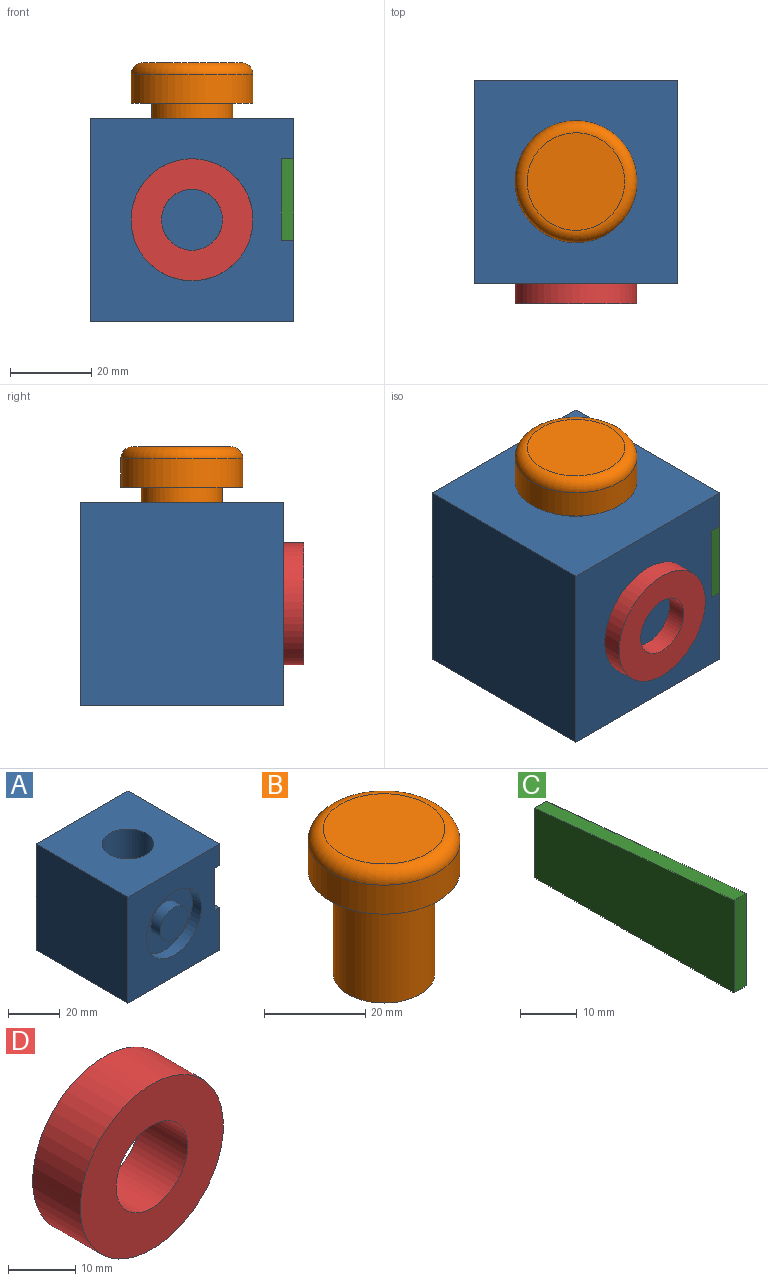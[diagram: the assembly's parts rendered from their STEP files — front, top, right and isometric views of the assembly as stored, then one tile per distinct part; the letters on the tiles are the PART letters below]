
ASSEMBLY  parts=4 mates=3
PART A: 16 faces, bbox 50x50x50 mm
  f0: plane 50x20mm, normal (1,0,0), area 1000mm2, adj f2,f4,f6,f13
  f1: plane 50x15mm, normal (1,0,0), area 625mm2, adj f2,f4,f5,f14
  f2: plane 50x50mm, normal (0,1,0), area 2455mm2, adj f0,f1,f3,f5,f6,f13,f14,f15
  f3: plane 50x50mm, normal (-1,0,0), area 2500mm2, adj f2,f4,f5,f6
  f4: plane 50x50mm, normal (0,-1,0), area 1733.1mm2, adj f0,f1,f3,f5,f6,f10,f13,f14
  f5: plane 50x50mm, normal (0,0,1), area 2185.8mm2, adj f1,f2,f3,f4,f7
  f6: plane 50x50mm, normal (0,0,-1), area 2500mm2, adj f0,f2,f3,f4
  f7: cylinder r=10mm len=25mm, axis (0,0,1), area 1570.8mm2, adj f5,f8
  f8: plane 20x20mm, normal (0,0,1), area 314.2mm2, adj f7
  f9: cylinder r=7.5mm len=15mm, axis (0,-1,0), area 235.6mm2, adj f11,f12
  f10: cylinder r=15mm len=30mm, axis (0,-1,0), area 471.2mm2, adj f4,f11
  f11: plane 30x30mm, normal (0,-1,0), area 530.1mm2, adj f9,f10
  f12: plane 15x15mm, normal (0,-1,0), area 176.7mm2, adj f9
  f13: plane 50x3mm, normal (0,0,1), area 150mm2, adj f0,f2,f4,f15
  f14: plane 50x5mm, normal (0,-0.1,-1), area 150.7mm2, adj f1,f2,f4,f15
  f15: plane 50x20mm, normal (1,0,0), area 875mm2, adj f2,f4,f13,f14
PART B: 6 faces, bbox 32.5x32.5x35 mm
  f0: cylinder r=10mm len=25mm, axis (0,0,-1), area 1570.8mm2, adj f1,f4
  f1: plane 20x20mm, normal (0,0,-1), area 314.2mm2, adj f0
  f2: cylinder r=15mm len=30mm, axis (0,0,-1), area 659.7mm2, adj f4,f5
  f3: plane 24x24mm, normal (0,0,1), area 452.4mm2, adj f5
  f4: plane 30x30mm, normal (0,0,-1), area 392.7mm2, adj f0,f2
  f5: torus R=12mm, axis (0,0,1), area 411.9mm2, adj f2,f3
PART C: 6 faces, bbox 3x50x20 mm
  f0: plane 50x3mm, normal (0,0,-1), area 150mm2, adj f1,f3,f4,f5
  f1: plane 15x3mm, normal (0,1,0), area 45mm2, adj f0,f2,f4,f5
  f2: plane 50x5mm, normal (0,0.1,1), area 150.7mm2, adj f1,f3,f4,f5
  f3: plane 20x3mm, normal (0,-1,0), area 60mm2, adj f0,f2,f4,f5
  f4: plane 50x20mm, normal (1,0,0), area 875mm2, adj f0,f1,f2,f3
  f5: plane 50x20mm, normal (-1,0,0), area 875mm2, adj f0,f1,f2,f3
PART D: 4 faces, bbox 30x10x30 mm
  f0: cylinder r=7.5mm len=15mm, axis (0,1,0), area 471.2mm2, adj f2,f3
  f1: cylinder r=15mm len=30mm, axis (0,1,0), area 942.5mm2, adj f2,f3
  f2: plane 30x30mm, normal (0,-1,0), area 530.1mm2, adj f0,f1
  f3: plane 30x30mm, normal (0,1,0), area 530.1mm2, adj f0,f1
PLACE A rot(axis=(0.77,-0.38,-0.51),0deg) t=(-76.53,49.64,-48.83)mm
PLACE B rot(axis=(0.77,-0.38,-0.51),0deg) t=(-76.53,49.64,-20.17)mm
PLACE C rot(axis=(0.77,-0.38,-0.51),0deg) t=(-54.53,74.64,-28.83)mm
PLACE D rot(axis=(0.77,-0.38,-0.51),0deg) t=(-76.53,29.64,-23.83)mm
MATE fastened A.f15 <-> C.f5  axis (1,0,0) through (-54.53,24.64,-18.83)mm
MATE fastened A.f9 <-> D.f1  axis (0,-1,0) through (-76.53,29.64,-23.83)mm
MATE slider A.f7 <-> B.f0  axis (0,0,1) through (-76.53,49.64,-23.83)mm
